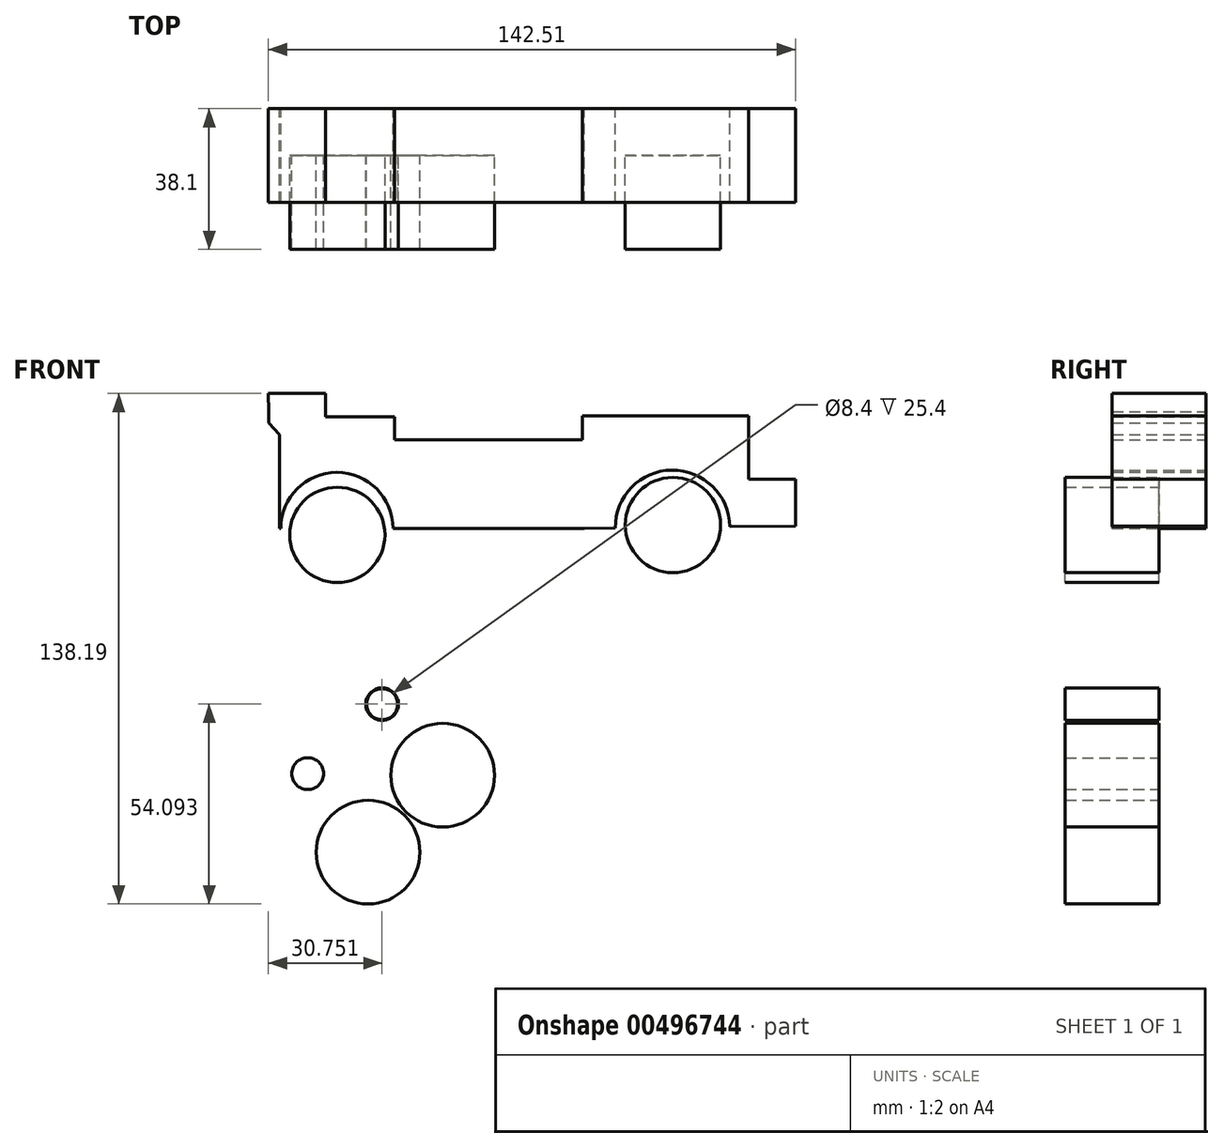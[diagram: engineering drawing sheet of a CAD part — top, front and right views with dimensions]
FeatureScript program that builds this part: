
annotation { "Feature Type Name" : "Feature", "Feature Type Description" : "" }
export const myFeature = defineFeature(function(context is Context, id is Id, definition is map)
    precondition{}
    {
        {
            var Q0;
            Q0=qCreatedBy(makeId("Front.planeOp"),FACE);
            var sketch = newSketch(context, id + "F0", { "sketchPlane" : qUnion([Q0])});
            skLineSegment(sketch, "E0", {"start": v(-70.58, 52.62) * mm, "end": v(-70.58, 27.22) * mm});
            skLineSegment(sketch, "E1", {"start": v(-70.58, 52.62) * mm, "end": v(-73.42, 55.74) * mm});
            skLineSegment(sketch, "E2", {"start": v(-73.42, 55.74) * mm, "end": v(-73.42, 58.86) * mm});
            skLineSegment(sketch, "E3", {"start": v(-70.58, 27.22) * mm, "end": v(-64.34, 27.22) * mm});
            skLineSegment(sketch, "E4", {"start": v(-45.32, 27.22) * mm, "end": v(11.83, 27.22) * mm});
            skLineSegment(sketch, "E5", {"start": v(-39.48, 57.69) * mm, "end": v(-39.48, 43.1) * mm});
            skLineSegment(sketch, "E6", {"start": v(-39.48, 43.1) * mm, "end": v(11.32, 43.1) * mm});
            skLineSegment(sketch, "E7", {"start": v(56.27, 40.58) * mm, "end": v(68.97, 40.58) * mm});
            skLineSegment(sketch, "E8", {"start": v(68.97, 40.58) * mm, "end": v(68.97, 27.88) * mm});
            skLineSegment(sketch, "E9", {"start": v(68.97, 27.88) * mm, "end": v(11.83, 27.22) * mm});
            skLineSegment(sketch, "E10", {"start": v(11.32, 43.1) * mm, "end": v(11.32, 57.69) * mm});
            skLineSegment(sketch, "E11", {"start": v(-73.54, 63.73) * mm, "end": v(-73.42, 58.86) * mm});
            skCircle(sketch, "E12", {"center": v(-55.03, 27.22) * mm, "radius": 15.18 * mm});
            skLineSegment(sketch, "E13.top", {"start": v(-58.08, 51.14) * mm, "end": v(-39.48, 51.14) * mm});
            skLineSegment(sketch, "E13.left", {"start": v(-58.08, 63.73) * mm, "end": v(-58.08, 51.14) * mm});
            skLineSegment(sketch, "E14", {"start": v(56.27, 40.58) * mm, "end": v(56.27, 57.69) * mm});
            skLineSegment(sketch, "E15", {"start": v(56.27, 57.69) * mm, "end": v(41.74, 57.69) * mm});
            skCircle(sketch, "E16", {"center": v(35.76, 27.5) * mm, "radius": 15.49 * mm});
            skLineSegment(sketch, "E17.bottom", {"start": v(-39.48, 51.14) * mm, "end": v(11.32, 51.14) * mm});
            skLineSegment(sketch, "E17.left", {"start": v(-39.48, 51.14) * mm, "end": v(-39.48, 43.1) * mm});
            skLineSegment(sketch, "E17.right", {"start": v(11.32, 51.14) * mm, "end": v(11.32, 43.1) * mm});
            skLineSegment(sketch, "E18.bottom", {"start": v(-58.08, 57.44) * mm, "end": v(-39.48, 57.44) * mm});
            skLineSegment(sketch, "E18.left", {"start": v(-58.08, 57.44) * mm, "end": v(-58.08, 51.14) * mm});
            skLineSegment(sketch, "E18.right", {"start": v(-39.48, 57.44) * mm, "end": v(-39.48, 51.14) * mm});
            skFitSpline(sketch, "E19", {"points": [v(-39.48, 57.44) * mm, v(23.16, 57.69) * mm], "startDerivative": vector(40.93, 75.96) * mm, "endDerivative": vector(55.55, -27.6) * mm});
            skLineSegment(sketch, "E20", {"start": v(-58.08, 63.73) * mm, "end": v(-73.54, 63.73) * mm});
            skLineSegment(sketch, "E21", {"start": v(-45.32, 27.22) * mm, "end": v(-64.34, 27.22) * mm});
            skLineSegment(sketch, "E22", {"start": v(41.74, 57.69) * mm, "end": v(11.32, 57.69) * mm});
            skSolve(sketch);
        }
        {
            var Q0;
            {var subQ10=sQuery(id+"F0.wireOp",EDGE,"E0");Q0=makeQuery(id+"F0.imprint","IMPRINT",FACE,{"disambiguationData":[TD([[makeQuery(id+"F0.imprint","IMPRINT",EDGE,{"derivedFrom":subQ10}),1.0]])]});}
            var Q1;
            {var subQ1=sQuery(id+"F0.wireOp",EDGE,"E10");Q1=makeQuery(id+"F0.imprint","IMPRINT",FACE,{"disambiguationData":[TD([[makeQuery(id+"F0.imprint","IMPRINT",EDGE,{"derivedFrom":subQ1}),1.0]])]});}
            var Q2;
            Q2=makeQuery(id+"F0.imprint","IMPRINT",FACE,{"disambiguationData":[TD([[makeQuery(id+"F0.imprint","IMPRINT",EDGE,{"derivedFrom":sQuery(id+"F0.wireOp",EDGE,"E17.bottom")}),-1.0]])]});
            var Q3;
            Q3=makeQuery(id+"F0.imprint","IMPRINT",FACE,{"disambiguationData":[TD([[makeQuery(id+"F0.imprint","IMPRINT",EDGE,{"derivedFrom":sQuery(id+"F0.wireOp",EDGE,"E18.bottom")}),-1.0]])]});
            extrude(context, id + "F1", {"entities" : qUnion([Q0, Q1, Q2, Q3]), "endBound" : BoundingType.SYMMETRIC, "depth" : 25.4 * mm});
        }
        {
            var Q0;
            Q0=qCreatedBy(makeId("Front.planeOp"),FACE);
            var sketch = newSketch(context, id + "F2", { "sketchPlane" : qUnion([Q0])});
            skCircle(sketch, "E23", {"center": v(-54.9, 25.46) * mm, "radius": 12.9 * mm});
            skCircle(sketch, "E24", {"center": v(35.87, 28.1) * mm, "radius": 12.9 * mm});
            skCircle(sketch, "E25", {"center": v(-42.79, -20.37) * mm, "radius": 4.41 * mm});
            skCircle(sketch, "E26", {"center": v(-42.79, -20.37) * mm, "radius": 4.2 * mm});
            skCircle(sketch, "E27", {"center": v(-62.92, -39.17) * mm, "radius": 4.31 * mm});
            skCircle(sketch, "E28", {"center": v(-46.59, -60.42) * mm, "radius": 14.03 * mm});
            skCircle(sketch, "E29", {"center": v(-26.41, -39.6) * mm, "radius": 14.03 * mm});
            skSolve(sketch);
        }
        {
            var Q0;
            Q0 = qSketchRegion(id + "F2", true);
            extrude(context, id + "F3", {"entities" : qUnion([Q0]), "depth" : 25.4 * mm});
        }
    });
